# Revit family: PlumbingFixture_GroheLimited_RoughInSet_45984001_METRIC1
name_source: partatom
category: Plumbing Fixtures
revit_build: Autodesk Revit 2015 (Build: 20160512_1515(x64)
units: mm (PartAtom-declared; Revit-internal decimal feet)

## types (1)
- 23451001
    ADACompliant = No
    Assembly Code = D2010
    AssetType = Fixed
    BIMObjectName = PlumbingFixture_GroheLimited_RoughInSet_45984001_METRIC
    Brass = Brass
    CW Connection = No
    CWFU = 4.5
    ClassificationName = Uniclass2015
    ClassificationValue = Pr_40_20_87_82
    ColdWaterConnectionDiameter = 25 mm  [stored 0.082021 ft]
    Color = Brass & PVC
    Cost = 0 $
    Default Elevation = 0 mm  [stored 0 ft]
    Description = Rough-in set ½". for floor-mounted bath mixers/spouts and shower mixers. without finishing trim set. installation plate with 360° horizontal and 3° vertical adjustment. installation depth 53-157 mm for bath mixers/spouts, depth compensation 104 mm. installation depth 65-157 mm for shower. mixers, depth compensation 92 mm. two ½" female connections (hot/cold supplies). flushing plug. acoustic isolation mat. gasket included. fixing material.
    DurationUnit = Years
    Ecojoy = No
    ExpectedLife = 0
    Features = Rough-in set ½". for floor-mounted bath mixers/spouts and shower mixers. without finishing trim set. installation plate with 360° horizontal and 3° vertical adjustment. installation depth 53-157 mm for bath mixers/spouts, depth compensation 104 mm. installation depth 65-157 mm for shower. mixers, depth compensation 92 mm. two ½" female connections (hot/cold supplies). flushing plug. acoustic isolation mat. gasket included. fixing material.
    Finish = Brass & PVC
    HW Connection = No
    HWFU = 4.5
    HotWaterConnectionDiameter = 25 mm  [stored 0.082021 ft]
    IfcExportAs = IfcPipeFitting
    IfcExportType = IfcPipeFittingType
    Keynote = N13
    LowEmittingMaterial = No
    Manufacturer = Grohe Limited
    ManufacturerName = Grohe Limited
    MasterformatNumber = 01 52 19
    MasterformatTitle = Sanitary Facilities
    Material = Brass & PVC
    Model = Rough-in set ½"
    ModelNumber = 45984001
    ModelReference = Rough-in set ½"
    NBSDescription = Water supply fittings for sinks;
    NBSObjectName = Grohe Limited - Water supply fittings for sinks;
    NBSReference = 45-35-70/345
    NominalDepth = 0 mm  [stored 0 ft]
    NominalHeight = 0 mm  [stored 0 ft]
    NominalLength = 0 mm  [stored 0 ft]
    PrimaryMaterial = Grohe-Black
    ProductDocumentationLink = https://www.grohe.com
    ProductPageURL = https://www.grohe.com
    ProductionYear = 2017
    Type Comments = 45984001
    TypeName = Rough-in set ½"
    URL = www.grohe.com
    Vent Connection = No
    WFU = 0
    WarrantyDurationUnit = Years
    Waste Connection = No
    _BSBibleVersion = 14
    _BimSpecGuid = 0
    _CurrentRevision = 1
    _DistributedBy = www.bimstore.co.uk

note: [stored X ft] marks values corroborated as IEEE doubles in the binary element streams (Revit-internal decimal feet)

## geometry (parser evidence)
native form markers: Sweep x2
no freeform markers — native parametric forms only
